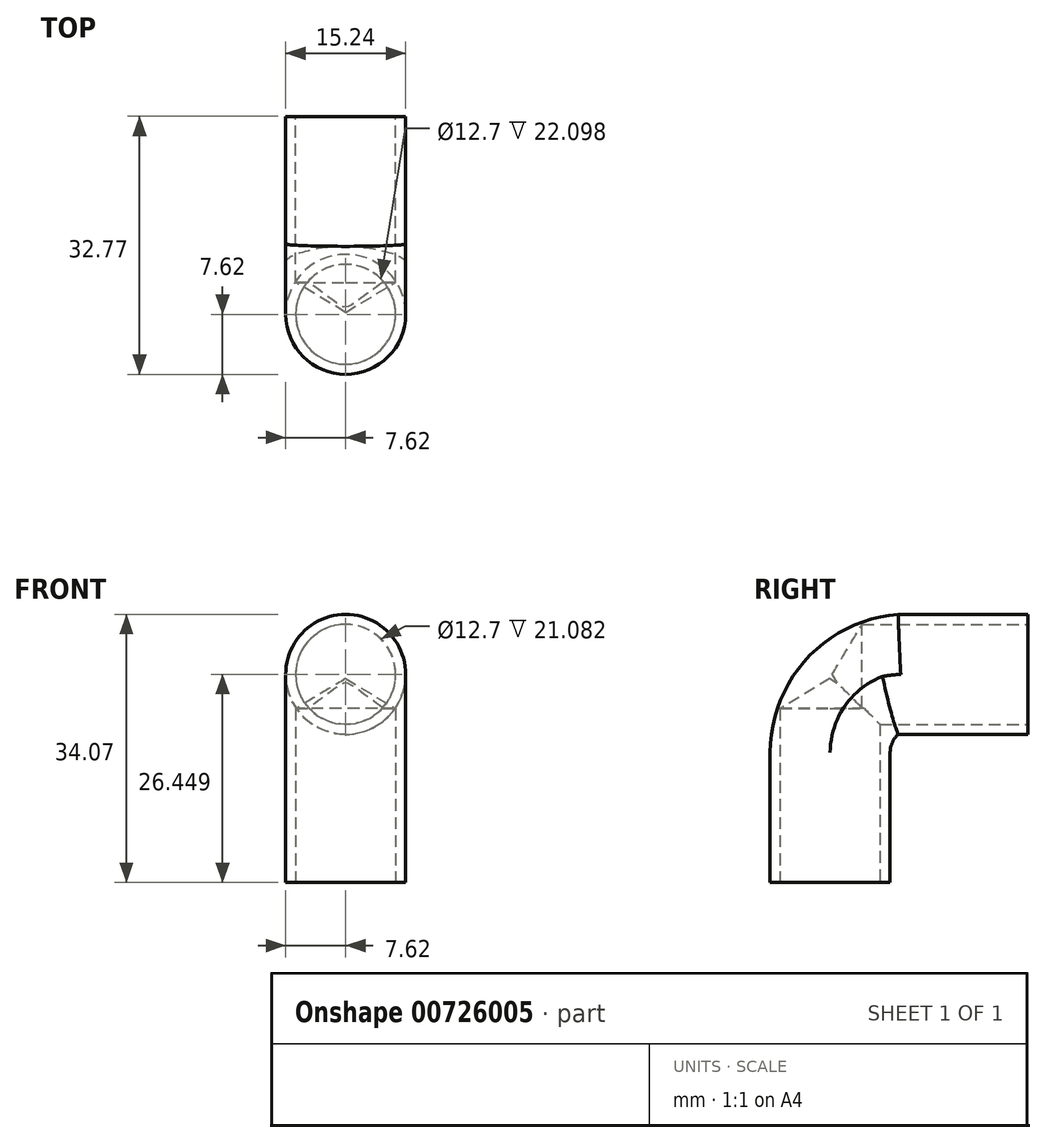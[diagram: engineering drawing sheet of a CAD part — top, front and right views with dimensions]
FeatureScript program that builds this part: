
annotation { "Feature Type Name" : "Feature", "Feature Type Description" : "" }
export const myFeature = defineFeature(function(context is Context, id is Id, definition is map)
    precondition{}
    {
        {
            var Q0;
            Q0=qCreatedBy(makeId("Right.planeOp"),FACE);
            var sketch = newSketch(context, id + "F0", { "sketchPlane" : qUnion([Q0])});
            skLineSegment(sketch, "E0.bottom", {"start": v(7.62, -7.62) * mm, "end": v(-7.62, -7.62) * mm});
            skLineSegment(sketch, "E0.top", {"start": v(7.62, 7.62) * mm, "end": v(-7.62, 7.62) * mm});
            skLineSegment(sketch, "E0.left", {"start": v(7.62, -7.62) * mm, "end": v(7.62, 7.62) * mm});
            skLineSegment(sketch, "E0.right", {"start": v(-7.62, -7.62) * mm, "end": v(-7.62, 7.62) * mm});
            skPoint(sketch, "E0.middle", {"position": v(0, 0) * mm});
            skLineSegment(sketch, "E1.bottom", {"start": v(25.15, 11.2) * mm, "end": v(9.9, 11.2) * mm});
            skLineSegment(sketch, "E1.top", {"start": v(25.15, 26.45) * mm, "end": v(9.9, 26.45) * mm});
            skLineSegment(sketch, "E1.left", {"start": v(25.15, 11.2) * mm, "end": v(25.15, 26.45) * mm});
            skLineSegment(sketch, "E1.right", {"start": v(9.9, 11.2) * mm, "end": v(9.9, 26.45) * mm});
            skPoint(sketch, "E1.middle", {"position": v(17.53, 18.83) * mm});
            skLineSegment(sketch, "E2", {"start": v(7.62, 7.62) * mm, "end": v(7.62, 8.9) * mm});
            skLineSegment(sketch, "E3", {"start": v(9.9, 11.2) * mm, "end": v(8.64, 11.2) * mm});
            skLineSegment(sketch, "E4", {"start": v(9.9, 26.45) * mm, "end": v(8.64, 26.45) * mm});
            skLineSegment(sketch, "E5", {"start": v(-7.62, 7.62) * mm, "end": v(-7.62, 8.9) * mm});
            skArc(sketch, "E6", {"start": v(7.62, 8.9) * mm, "mid": v(7.89, 10.16) * mm, "end": v(8.64, 11.2) * mm});
            skArc(sketch, "E7", {"start": v(-7.62, 8.9) * mm, "mid": v(-2.93, 20.85) * mm, "end": v(8.64, 26.45) * mm});
            skSolve(sketch);
        }
        {
            var Q0;
            Q0=makeQuery(id+"F0.imprint","IMPRINT",FACE,{"disambiguationData":[TD([[makeQuery(id+"F0.imprint","IMPRINT",EDGE,{"derivedFrom":sQuery(id+"F0.wireOp",EDGE,"E0.bottom")}),-1.0]])]});
            var Q1;
            Q1=makeQuery(id+"F0.imprint","IMPRINT",FACE,{"disambiguationData":[TD([[makeQuery(id+"F0.imprint","IMPRINT",EDGE,{"derivedFrom":sQuery(id+"F0.wireOp",EDGE,"E0.top")}),-1.0]])]});
            var Q2;
            Q2=makeQuery(id+"F0.imprint","IMPRINT",FACE,{"disambiguationData":[TD([[makeQuery(id+"F0.imprint","IMPRINT",EDGE,{"derivedFrom":sQuery(id+"F0.wireOp",EDGE,"E1.bottom")}),-1.0]])]});
            extrude(context, id + "F1", {"entities" : qUnion([Q0, Q1, Q2]), "endBound" : BoundingType.SYMMETRIC, "depth" : 15.24 * mm, "offsetDistance" : 25.4 * mm});
        }
        {
            var Q0;
            Q0=makeQuery(id+"F1.opExtrude","CAP_EDGE",EDGE,{"disambiguationData":[OSD([sQuery(id+"F0.wireOp",EDGE,"E0.right"),sQuery(id+"F0.wireOp",EDGE,"E5")])],"isStart":false});
            var Q1;
            Q1=makeQuery(id+"F1.opExtrude","CAP_EDGE",EDGE,{"disambiguationData":[OSD([sQuery(id+"F0.wireOp",EDGE,"9c886f39-38b8-4ab7-a82a-ee3d060ac1b0")])],"isStart":false});
            var Q2;
            Q2=makeQuery(id+"F1.opExtrude","CAP_EDGE",EDGE,{"disambiguationData":[OSD([sQuery(id+"F0.wireOp",EDGE,"E1.top"),sQuery(id+"F0.wireOp",EDGE,"E4")])],"isStart":false});
            var Q3;
            Q3=makeQuery(id+"F1.opExtrude","CAP_EDGE",EDGE,{"disambiguationData":[OSD([sQuery(id+"F0.wireOp",EDGE,"E0.right"),sQuery(id+"F0.wireOp",EDGE,"E5")])],"isStart":true});
            var Q4;
            Q4=makeQuery(id+"F1.opExtrude","CAP_EDGE",EDGE,{"disambiguationData":[OSD([sQuery(id+"F0.wireOp",EDGE,"9c886f39-38b8-4ab7-a82a-ee3d060ac1b0")])],"isStart":true});
            var Q5;
            Q5=makeQuery(id+"F1.opExtrude","CAP_EDGE",EDGE,{"disambiguationData":[OSD([sQuery(id+"F0.wireOp",EDGE,"E1.top"),sQuery(id+"F0.wireOp",EDGE,"E4")])],"isStart":true});
            var Q6;
            Q6=makeQuery(id+"F1.opExtrude","CAP_EDGE",EDGE,{"disambiguationData":[OSD([sQuery(id+"F0.wireOp",EDGE,"E0.left"),sQuery(id+"F0.wireOp",EDGE,"E2")])],"isStart":true});
            var Q7;
            Q7=makeQuery(id+"F1.opExtrude","CAP_EDGE",EDGE,{"disambiguationData":[OSD([sQuery(id+"F0.wireOp",EDGE,"aa0a6e58-a980-41a9-83db-c4c254e78a4c")])],"isStart":true});
            var Q8;
            Q8=makeQuery(id+"F1.opExtrude","CAP_EDGE",EDGE,{"disambiguationData":[OSD([sQuery(id+"F0.wireOp",EDGE,"E1.bottom"),sQuery(id+"F0.wireOp",EDGE,"E3")])],"isStart":true});
            var Q9;
            Q9=makeQuery(id+"F1.opExtrude","CAP_EDGE",EDGE,{"disambiguationData":[OSD([sQuery(id+"F0.wireOp",EDGE,"E1.bottom"),sQuery(id+"F0.wireOp",EDGE,"E3")])],"isStart":false});
            var Q10;
            Q10=makeQuery(id+"F1.opExtrude","CAP_EDGE",EDGE,{"disambiguationData":[OSD([sQuery(id+"F0.wireOp",EDGE,"aa0a6e58-a980-41a9-83db-c4c254e78a4c")])],"isStart":false});
            var Q11;
            Q11=makeQuery(id+"F1.opExtrude","CAP_EDGE",EDGE,{"disambiguationData":[OSD([sQuery(id+"F0.wireOp",EDGE,"E0.left"),sQuery(id+"F0.wireOp",EDGE,"E2")])],"isStart":false});
            fillet(context, id + "F2", {"entities" : qUnion([Q0, Q1, Q2, Q3, Q4, Q5, Q6, Q7, Q8, Q9, Q10, Q11]), "radius" : 7.62 * mm, "tangentPropagation" : true, "allowEdgeOverflow" : false});
        }
        {
            var Q0;
            Q0=makeQuery(id+"F1.opExtrude","SWEPT_FACE",FACE,{"disambiguationData":[OSD([sQuery(id+"F0.wireOp",EDGE,"E1.left")])]});
            var sketch = newSketch(context, id + "F3", { "sketchPlane" : qUnion([Q0])});
            skPoint(sketch, "E8", {"position": v(0, 18.83) * mm});
            skSolve(sketch);
        }
        {
            var Q0;
            Q0=sQuery(id+"F3.wireOp",VERTEX,"E8");
            var Q1;
            Q1=makeQuery(id+"F1.opExtrude","SWEPT_BODY",BODY,{"disambiguationData":[OSD([sQuery(id+"F0.wireOp",EDGE,"E0.bottom"),sQuery(id+"F0.wireOp",EDGE,"E0.left"),sQuery(id+"F0.wireOp",EDGE,"E0.right"),sQuery(id+"F0.wireOp",EDGE,"E1.bottom"),sQuery(id+"F0.wireOp",EDGE,"E1.top"),sQuery(id+"F0.wireOp",EDGE,"E1.left"),sQuery(id+"F0.wireOp",EDGE,"E2"),sQuery(id+"F0.wireOp",EDGE,"E3"),sQuery(id+"F0.wireOp",EDGE,"E4"),sQuery(id+"F0.wireOp",EDGE,"E5"),sQuery(id+"F0.wireOp",EDGE,"aa0a6e58-a980-41a9-83db-c4c254e78a4c"),sQuery(id+"F0.wireOp",EDGE,"9c886f39-38b8-4ab7-a82a-ee3d060ac1b0")])]});
            hole(context, id + "F4", {"style" : HoleStyle.C_BORE, "endStyle" : HoleEndStyle.BLIND, "holeDiameter" : 12.7 * mm, "cBoreDiameter" : 50.8 * mm, "cBoreDepth" : 0 * mm, "majorDiameter" : 6.35 * mm, "holeDepth" : 21.08 * mm, "isTappedThrough" : true, "tappedDepth" : 12.7 * mm, "tapClearance" : 3, "startFromSketch" : true, "locations" : qUnion([Q0]), "scope" : qUnion([Q1])});
        }
        {
            var Q0;
            Q0=makeQuery(id+"F1.opExtrude","SWEPT_FACE",FACE,{"disambiguationData":[OSD([sQuery(id+"F0.wireOp",EDGE,"E0.bottom")])]});
            var sketch = newSketch(context, id + "F5", { "sketchPlane" : qUnion([Q0])});
            skPoint(sketch, "E9", {"position": v(0, 0) * mm});
            skSolve(sketch);
        }
        {
            var Q0;
            Q0=sQuery(id+"F5.wireOp",VERTEX,"E9");
            var Q1;
            Q1=makeQuery(id+"F1.opExtrude","SWEPT_BODY",BODY,{"disambiguationData":[OSD([sQuery(id+"F0.wireOp",EDGE,"E0.bottom"),sQuery(id+"F0.wireOp",EDGE,"E0.left"),sQuery(id+"F0.wireOp",EDGE,"E0.right"),sQuery(id+"F0.wireOp",EDGE,"E1.bottom"),sQuery(id+"F0.wireOp",EDGE,"E1.top"),sQuery(id+"F0.wireOp",EDGE,"E1.left"),sQuery(id+"F0.wireOp",EDGE,"E2"),sQuery(id+"F0.wireOp",EDGE,"E3"),sQuery(id+"F0.wireOp",EDGE,"E4"),sQuery(id+"F0.wireOp",EDGE,"E5"),sQuery(id+"F0.wireOp",EDGE,"aa0a6e58-a980-41a9-83db-c4c254e78a4c"),sQuery(id+"F0.wireOp",EDGE,"9c886f39-38b8-4ab7-a82a-ee3d060ac1b0")])]});
            hole(context, id + "F6", {"style" : HoleStyle.C_BORE, "endStyle" : HoleEndStyle.BLIND, "holeDiameter" : 12.7 * mm, "cBoreDiameter" : 50.8 * mm, "cBoreDepth" : 0 * mm, "majorDiameter" : 6.35 * mm, "holeDepth" : 22.1 * mm, "isTappedThrough" : true, "tappedDepth" : 12.7 * mm, "tapClearance" : 3, "startFromSketch" : true, "locations" : qUnion([Q0]), "scope" : qUnion([Q1])});
        }
    });
